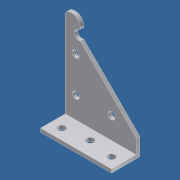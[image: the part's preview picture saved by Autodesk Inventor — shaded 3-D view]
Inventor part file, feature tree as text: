
AUTODESK INVENTOR PART (.ipt)
format: ipt  version: unknown  size: 267,264 bytes
history: native  units: in
note: dims shown in document units (in); Inventor stores cm internally (conversion verified against a paired STEP export)
features: sketch x10, plane x7, extrude x5, hole x5, fillet x1
ambient origin geometry x8: Origin, YZ Plane, XZ Plane, XY Plane, X Axis, Y Axis, Z Axis, Center Point
bodies: Solid1 (feature_tree)
feature tree (28):
  sketch  "Sketch1"  dims[d0=2.5in d1=0.125in]
  plane  "Work Plane1"
  extrude  "Extrusion2"  Depth=0.125in
  plane  "Work Plane4"
  extrude  "Extrusion3"  Depth=2.875in TaperAngle=0.0deg
  plane  "Work Plane3"
  hole  "Hole1"  [1 undecoded]
  plane  "Work Plane2"
  extrude  "Extrusion4"  Depth=0.25in
  plane  "Work Plane6"
  hole  "Hole2"  [1 undecoded]
  plane  "Work Plane5"
  hole  "Hole3"  [1 undecoded]
  extrude  "Extrusion5"  Depth=0.875in
  plane  "Work Plane7"
  hole  "Hole4"  [1 undecoded]
  fillet  "Fillet2"  Radius=0.375in
  extrude  "Extrusion7"  Depth=0.375in
  hole  "Hole5"  [1 undecoded]
  sketch  "Sketch2"  dims[d4=0.125in d5=2.875in d6=0.0in]
  sketch  "Sketch3"  dims[d7=0.5in d8=45.0deg]
  sketch  "Sketch4"  dims[d9=2.875in d10=0.0in d11=0.25in]
  sketch  "Sketch5"  dims[d12=0.4687in]
  sketch  "Sketch6"  dims[d13=0.3124in d14=0.75in d15=0.375in d16=0.25in d17=0.5635in d18=1.0in d19=0.8108in d20=0.625in d21=0.2187in]
  sketch  "Sketch7"  dims[d22=0.125in d23=0.0in d25=0.375in]
  sketch  "Sketch9"  dims[d26=1.25in d27=0.875in]
  sketch  "Sketch10"  dims[d28=0.875in d29=1.25in]
  sketch  "Sketch11"  dims[d30=0.25in d31=0.75in d32=0.375in d33=0.25in d34=0.5635in d35=1.0in d36=0.8108in d37=0.375in d38=0.375in d39=1.25in d40=0.125in d41=0.375in d42=0.375in d43=0.25in d44=0.75in d45=0.375in d46=0.25in d47=0.5635in d48=1.0in d49=0.8108in d50=0.125in d51=0.0in d55=0.375in d56=0.125in d57=0.375in d58=0.375in d59=0.25in d60=0.75in d61=0.375in d62=0.25in d63=0.5635in d64=1.0in d65=0.8108in d66=0.1in d67=0.125in d68=0.875in d69=0.0in d70=0.375in d71=0.375in d72=0.375in d73=0.375in d74=0.125in d75=1.25in d76=0.25in d77=0.75in d78=0.375in d79=0.25in d80=0.5635in d81=1.0in d82=0.8108in]
note: 5 required parameter values undecoded (feature->parameter linkage not recoverable at this tier; creation-order binding heuristic only, values carry confidence <= 0.55)
